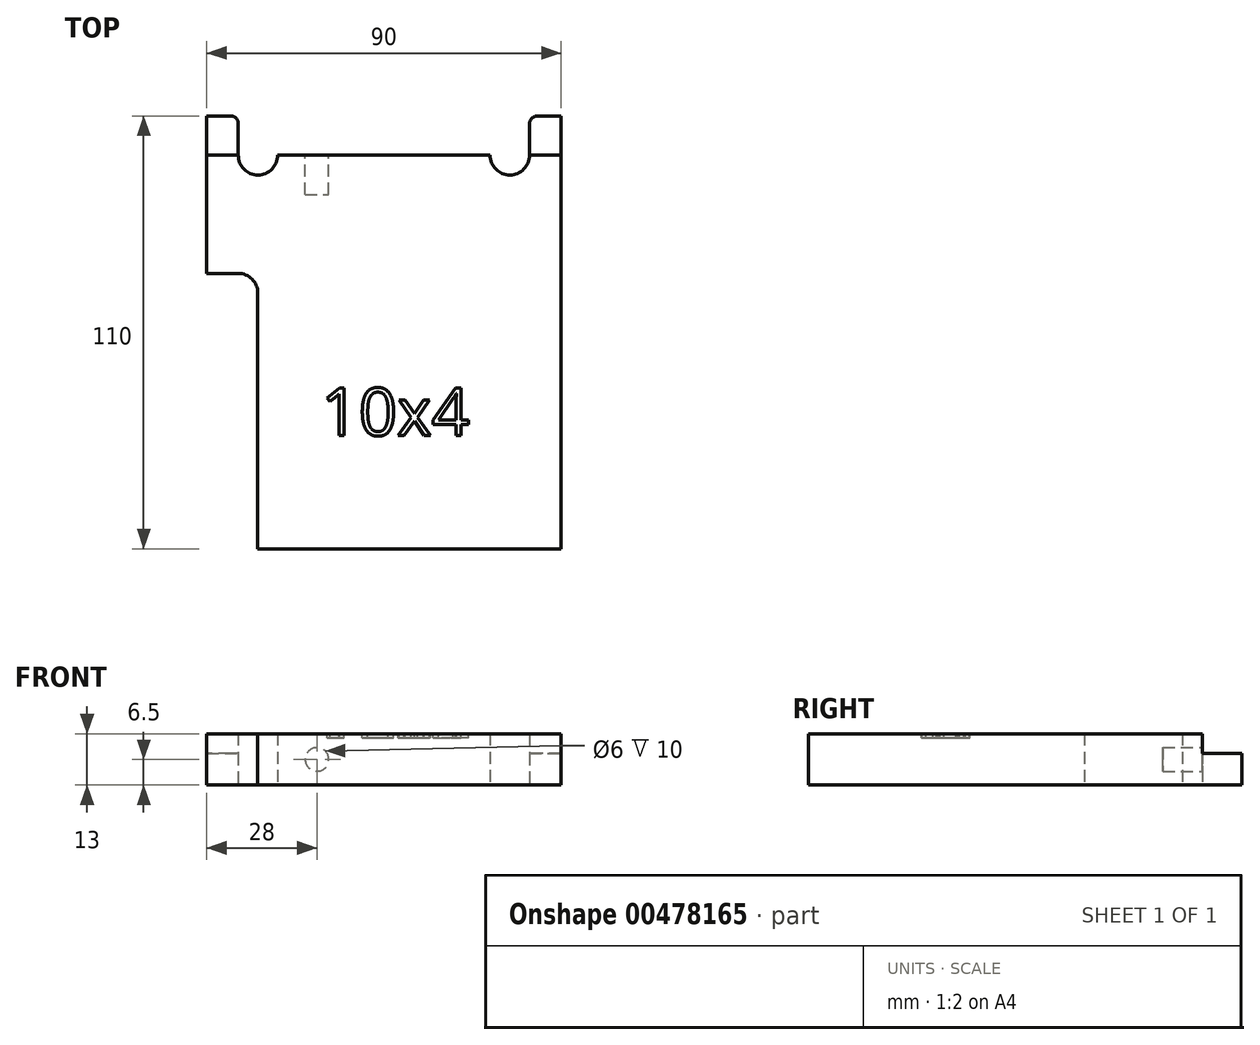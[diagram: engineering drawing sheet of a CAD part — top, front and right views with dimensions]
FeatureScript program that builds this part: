
annotation { "Feature Type Name" : "Feature", "Feature Type Description" : "" }
export const myFeature = defineFeature(function(context is Context, id is Id, definition is map)
    precondition{}
    {
        {
            var Q0;
            Q0=qCreatedBy(makeId("Top.planeOp"),FACE);
            var sketch = newSketch(context, id + "F0", { "sketchPlane" : qUnion([Q0])});
            skLineSegment(sketch, "E0", {"start": v(-40.48, -10.08) * mm, "end": v(-32.51, -10.08) * mm});
            skLineSegment(sketch, "E1", {"start": v(-27.51, -15.08) * mm, "end": v(-27.51, -80.08) * mm});
            skLineSegment(sketch, "E2", {"start": v(-27.51, -80.08) * mm, "end": v(49.52, -80.08) * mm});
            skLineSegment(sketch, "E3", {"start": v(49.52, -80.08) * mm, "end": v(49.52, 29.92) * mm});
            skLineSegment(sketch, "E4", {"start": v(49.52, 29.92) * mm, "end": v(43.52, 29.92) * mm});
            skLineSegment(sketch, "E5", {"start": v(41.52, 27.92) * mm, "end": v(41.52, 19.92) * mm});
            skLineSegment(sketch, "E6", {"start": v(-32.48, 19.92) * mm, "end": v(-32.48, 27.92) * mm});
            skLineSegment(sketch, "E7", {"start": v(-34.48, 29.92) * mm, "end": v(-40.48, 29.92) * mm});
            skLineSegment(sketch, "E8", {"start": v(-40.48, 29.92) * mm, "end": v(-40.48, -10.08) * mm});
            skPoint(sketch, "E9.visualSharp", {"position": v(-27.51, -10.08) * mm});
            skArc(sketch, "E9.filletArc", {"start": v(-27.51, -15.08) * mm, "mid": v(-28.97, -11.54) * mm, "end": v(-32.51, -10.08) * mm});
            skPoint(sketch, "E10.visualSharp", {"position": v(-32.48, 29.92) * mm});
            skArc(sketch, "E10.filletArc", {"start": v(-32.48, 27.92) * mm, "mid": v(-33.07, 29.33) * mm, "end": v(-34.48, 29.92) * mm});
            skPoint(sketch, "E11.visualSharp", {"position": v(41.52, 29.92) * mm});
            skArc(sketch, "E11.filletArc", {"start": v(43.52, 29.92) * mm, "mid": v(42.1, 29.33) * mm, "end": v(41.52, 27.92) * mm});
            skArc(sketch, "E12", {"start": v(-32.48, 19.92) * mm, "mid": v(-27.48, 14.92) * mm, "end": v(-22.48, 19.92) * mm});
            skArc(sketch, "E13", {"start": v(31.52, 19.92) * mm, "mid": v(36.52, 14.92) * mm, "end": v(41.52, 19.92) * mm});
            skLineSegment(sketch, "E14", {"start": v(-22.48, 19.92) * mm, "end": v(31.52, 19.92) * mm});
            skSolve(sketch);
        }
        {
            var Q0;
            Q0=makeQuery(id+"F0.imprint","IMPRINT",FACE,{"disambiguationData":[TD([[makeQuery(id+"F0.imprint","IMPRINT",EDGE,{"derivedFrom":sQuery(id+"F0.wireOp",EDGE,"E0")}),1.0]])]});
            extrude(context, id + "F1", {"entities" : qUnion([Q0]), "depth" : 13 * mm});
        }
        {
            var Q0;
            Q0=makeQuery(id+"F1.opExtrude","CAP_FACE",FACE,{"disambiguationData":[OSD([sQuery(id+"F0.wireOp",EDGE,"E0"),sQuery(id+"F0.wireOp",EDGE,"E1"),sQuery(id+"F0.wireOp",EDGE,"E2"),sQuery(id+"F0.wireOp",EDGE,"E3"),sQuery(id+"F0.wireOp",EDGE,"E4"),sQuery(id+"F0.wireOp",EDGE,"E5"),sQuery(id+"F0.wireOp",EDGE,"mmM2Y2U2-RtFC-ikFc-wxJO-fWfLtijxp1iX"),sQuery(id+"F0.wireOp",EDGE,"E6"),sQuery(id+"F0.wireOp",EDGE,"E7"),sQuery(id+"F0.wireOp",EDGE,"E8"),sQuery(id+"F0.wireOp",EDGE,"E9.filletArc"),sQuery(id+"F0.wireOp",EDGE,"E10.filletArc"),sQuery(id+"F0.wireOp",EDGE,"E11.filletArc")])],"isStart":false});
            var sketch = newSketch(context, id + "F2", { "sketchPlane" : qUnion([Q0])});
            skLineSegment(sketch, "E15.bottom", {"start": v(-43.08, 34.42) * mm, "end": v(64.23, 34.42) * mm});
            skLineSegment(sketch, "E15.top", {"start": v(-43.08, 19.92) * mm, "end": v(64.23, 19.92) * mm});
            skLineSegment(sketch, "E15.left", {"start": v(-43.08, 34.42) * mm, "end": v(-43.08, 19.92) * mm});
            skLineSegment(sketch, "E15.right", {"start": v(64.23, 34.42) * mm, "end": v(64.23, 19.92) * mm});
            skSolve(sketch);
        }
        {
            var Q0;
            Q0=qSketchRegion(id+"F2",true);
            extrude(context, id + "F3", {"entities" : qUnion([Q0]), "operationType" : NewBodyOperationType.REMOVE, "oppositeDirection" : true, "depth" : 5 * mm});
        }
        {
            var Q0;
            Q0=makeQuery(id+"F1.opExtrude","SWEPT_FACE",FACE,{"disambiguationData":[OSD([sQuery(id+"F0.wireOp",EDGE,"E14")])]});
            var sketch = newSketch(context, id + "F4", { "sketchPlane" : qUnion([Q0])});
            skCircle(sketch, "E16", {"center": v(12.48, 6.5) * mm, "radius": 3 * mm});
            skSolve(sketch);
        }
        {
            var Q0;
            Q0=qSketchRegion(id+"F4",true);
            extrude(context, id + "F5", {"entities" : qUnion([Q0]), "operationType" : NewBodyOperationType.REMOVE, "oppositeDirection" : true, "depth" : 10 * mm});
        }
        {
            var Q0;
            Q0=makeQuery(id+"F1.opExtrude","CAP_FACE",FACE,{"disambiguationData":[OSD([sQuery(id+"F0.wireOp",EDGE,"E0"),sQuery(id+"F0.wireOp",EDGE,"E1"),sQuery(id+"F0.wireOp",EDGE,"E2"),sQuery(id+"F0.wireOp",EDGE,"E3"),sQuery(id+"F0.wireOp",EDGE,"E4"),sQuery(id+"F0.wireOp",EDGE,"E5"),sQuery(id+"F0.wireOp",EDGE,"E6"),sQuery(id+"F0.wireOp",EDGE,"E7"),sQuery(id+"F0.wireOp",EDGE,"E8"),sQuery(id+"F0.wireOp",EDGE,"E9.filletArc"),sQuery(id+"F0.wireOp",EDGE,"E10.filletArc"),sQuery(id+"F0.wireOp",EDGE,"E11.filletArc"),sQuery(id+"F0.wireOp",EDGE,"E12"),sQuery(id+"F0.wireOp",EDGE,"E13"),sQuery(id+"F0.wireOp",EDGE,"E14")])],"isStart":false});
            var sketch = newSketch(context, id + "F6", { "sketchPlane" : qUnion([Q0])});
            skText(sketch, "E17", { "text": "10x4", "fontName": "OpenSans-Regular.ttf"});
            const initialGuessF6  = {"E17": [-0.01145, -0.0513, 1, 0, 0.01214]};
            skSetInitialGuess(sketch, initialGuessF6);
            skSolve(sketch);
        }
        {
            var Q0;
            Q0=qSketchRegion(id+"F6",true);
            extrude(context, id + "F7", {"entities" : qUnion([Q0]), "operationType" : NewBodyOperationType.REMOVE, "oppositeDirection" : true, "depth" : 1 * mm});
        }
    });
